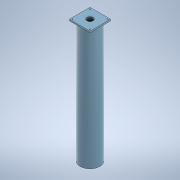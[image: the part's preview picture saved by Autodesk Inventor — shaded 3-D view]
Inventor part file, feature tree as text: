
AUTODESK INVENTOR PART (.ipt)
format: ipt  version: 2022 (Build 260153000, 153)  size: 136,192 bytes
history: native  units: mm
features: sketch x4, extrude x3, other x1, plane x1, hole x1
ambient origin geometry x8: Origin, YZ Plane, XZ Plane, XY Plane, X Axis, Y Axis, Z Axis, Center Point
bodies: Solid1 (feature_tree)
feature tree (10):
  other  "RaAxis.ipt"
  extrude  "Beam"  Depth=800.0mm TaperAngle=0.0deg
  plane  "Work Plane1"
  extrude  "Connector"  Depth=10.0mm TaperAngle=0.0deg
  extrude  "CableHole"  [1 undecoded]
  hole  "Hole2"  [1 undecoded]
  sketch  "Sketch1"  dims[d0=130.0mm d1=800.0mm d2=0.0mm]
  sketch  "Sketch2"  dims[d3=0.0mm d4=10.0mm d5=0.0mm]
  sketch  "Sketch6"  dims[d17=10.0mm d18=0.0mm]
  sketch  "Sketch8"  dims[d19=6.0mm d20=6.0mm d21=9.0mm d22=2.0mm d23=90.0deg d24=10.0mm d25=20.594885mm]
note: 2 required parameter values undecoded (feature->parameter linkage not recoverable at this tier; creation-order binding heuristic only, values carry confidence <= 0.55)
